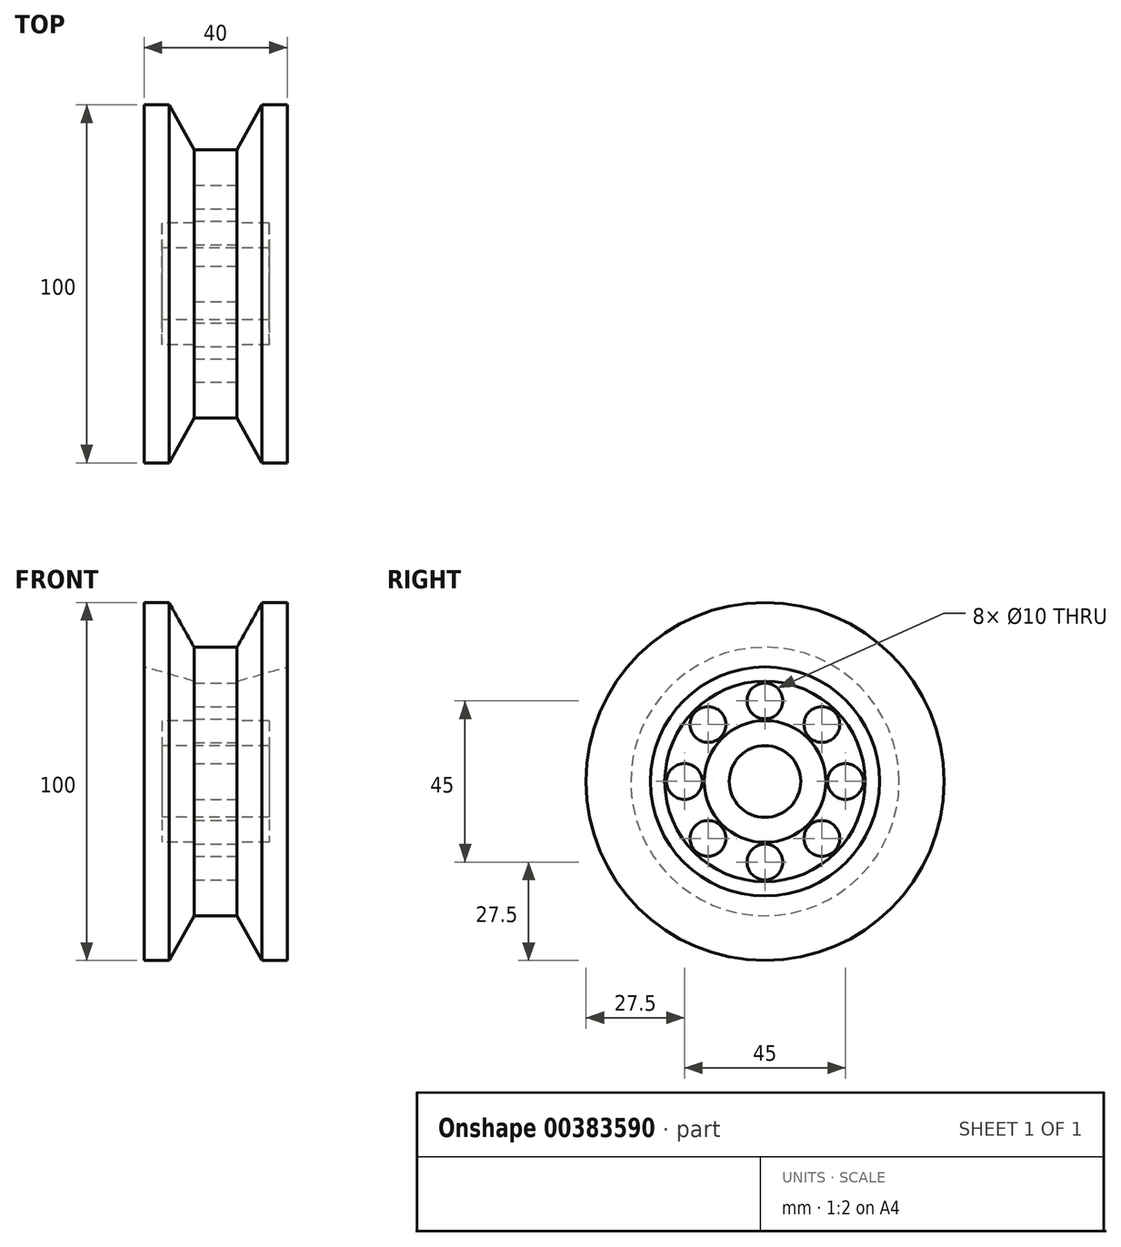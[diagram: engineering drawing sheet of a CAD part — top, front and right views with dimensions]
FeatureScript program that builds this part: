
annotation { "Feature Type Name" : "Feature", "Feature Type Description" : "" }
export const myFeature = defineFeature(function(context is Context, id is Id, definition is map)
    precondition{}
    {
        {
            var Q0;
            Q0=qCreatedBy(makeId("Front.planeOp"),FACE);
            var sketch = newSketch(context, id + "F0", { "sketchPlane" : qUnion([Q0])});
            skLineSegment(sketch, "E0", {"start": v(-20, 0) * mm, "end": v(20, 0) * mm});
            skLineSegment(sketch, "E1", {"start": v(20, 0) * mm, "end": v(20, -50) * mm});
            skLineSegment(sketch, "E2", {"start": v(20, -50) * mm, "end": v(13, -50) * mm});
            skLineSegment(sketch, "E3", {"start": v(13, -50) * mm, "end": v(6, -37.5) * mm});
            skLineSegment(sketch, "E4", {"start": v(6, -37.5) * mm, "end": v(-6, -37.5) * mm});
            skLineSegment(sketch, "E5", {"start": v(-6, -37.5) * mm, "end": v(-13, -50) * mm});
            skLineSegment(sketch, "E6", {"start": v(-13, -50) * mm, "end": v(-20, -50) * mm});
            skLineSegment(sketch, "E7", {"start": v(-20, -50) * mm, "end": v(-20, 0) * mm});
            skLineSegment(sketch, "E8", {"start": v(-15, 0) * mm, "end": v(-15, -17) * mm});
            skLineSegment(sketch, "E9", {"start": v(-15, -17) * mm, "end": v(15, -17) * mm});
            skLineSegment(sketch, "E10", {"start": v(15, -17) * mm, "end": v(15, 0) * mm});
            skLineSegment(sketch, "E11", {"start": v(-6, -28) * mm, "end": v(6, -28) * mm});
            skLineSegment(sketch, "E12", {"start": v(6, -28) * mm, "end": v(20, -32) * mm});
            skLineSegment(sketch, "E13", {"start": v(-6, -17) * mm, "end": v(-6, -28) * mm});
            skLineSegment(sketch, "E14", {"start": v(6, -17) * mm, "end": v(6, -28) * mm});
            skLineSegment(sketch, "E15", {"start": v(-15, -10) * mm, "end": v(15, -10) * mm});
            skLineSegment(sketch, "E16", {"start": v(-6, -28) * mm, "end": v(-20, -32) * mm});
            skSolve(sketch);
        }
        {
            var Q0;
            {var subQ7=sQuery(id+"F0.wireOp",EDGE,"E15");Q0=makeQuery(id+"F0.imprint","IMPRINT",FACE,{"disambiguationData":[TD([[makeQuery(id+"F0.imprint","IMPRINT",EDGE,{"derivedFrom":subQ7}),-1.0]])]});}
            var Q1;
            Q1=makeQuery(id+"F0.imprint","IMPRINT",FACE,{"disambiguationData":[TD([[makeQuery(id+"F0.imprint","IMPRINT",EDGE,{"derivedFrom":sQuery(id+"F0.wireOp",EDGE,"E11")}),1.0]])]});
            var Q2;
            {var subQ0=sQuery(id+"F0.wireOp",EDGE,"E2");Q2=makeQuery(id+"F0.imprint","IMPRINT",FACE,{"disambiguationData":[TD([[makeQuery(id+"F0.imprint","IMPRINT",EDGE,{"derivedFrom":subQ0}),-1.0]])]});}
            var Q3;
            Q3=sQuery(id+"F0.wireOp",EDGE,"E0");
            revolve(context, id + "F1", {"entities" : qUnion([Q0, Q1, Q2]), "axis" : qUnion([Q3]), "revolveType" : RevolveType.FULL});
        }
        {
            var Q0;
            Q0=makeQuery(id+"F1.opRevolve","SWEPT_FACE",FACE,{"disambiguationData":[OSD([sQuery(id+"F0.wireOp",EDGE,"E14")])]});
            var sketch = newSketch(context, id + "F2", { "sketchPlane" : qUnion([Q0])});
            skLineSegment(sketch, "E17", {"start": v(-55.64, 0) * mm, "end": v(57.98, 0) * mm});
            skLineSegment(sketch, "E18", {"start": v(0, 60.2) * mm, "end": v(0, -58.05) * mm});
            skLineSegment(sketch, "E19", {"start": v(-39.04, -39.04) * mm, "end": v(56.33, 56.33) * mm});
            skLineSegment(sketch, "E20", {"start": v(-56.33, 56.33) * mm, "end": v(50.25, -50.25) * mm});
            skCircle(sketch, "E21", {"center": v(0, 22.5) * mm, "radius": 5 * mm});
            skCircle(sketch, "E22", {"center": v(15.9, 15.9) * mm, "radius": 5 * mm});
            skCircle(sketch, "E23", {"center": v(22.5, 0) * mm, "radius": 5 * mm});
            skCircle(sketch, "E24", {"center": v(0, -22.5) * mm, "radius": 5 * mm});
            skCircle(sketch, "E25", {"center": v(15.9, -15.9) * mm, "radius": 5 * mm});
            skCircle(sketch, "E26.MirrorC", {"center": v(-15.9, 15.9) * mm, "radius": 5 * mm});
            skCircle(sketch, "E27.MirrorC", {"center": v(-22.5, 0) * mm, "radius": 5 * mm});
            skCircle(sketch, "E28.MirrorC", {"center": v(-15.9, -15.9) * mm, "radius": 5 * mm});
            skSolve(sketch);
        }
        {
            var Q0;
            Q0 = qSketchRegion(id + "F2", true);
            extrude(context, id + "F3", {"entities" : qUnion([Q0]), "operationType" : NewBodyOperationType.REMOVE, "oppositeDirection" : true, "depth" : 25 * mm});
        }
    });
